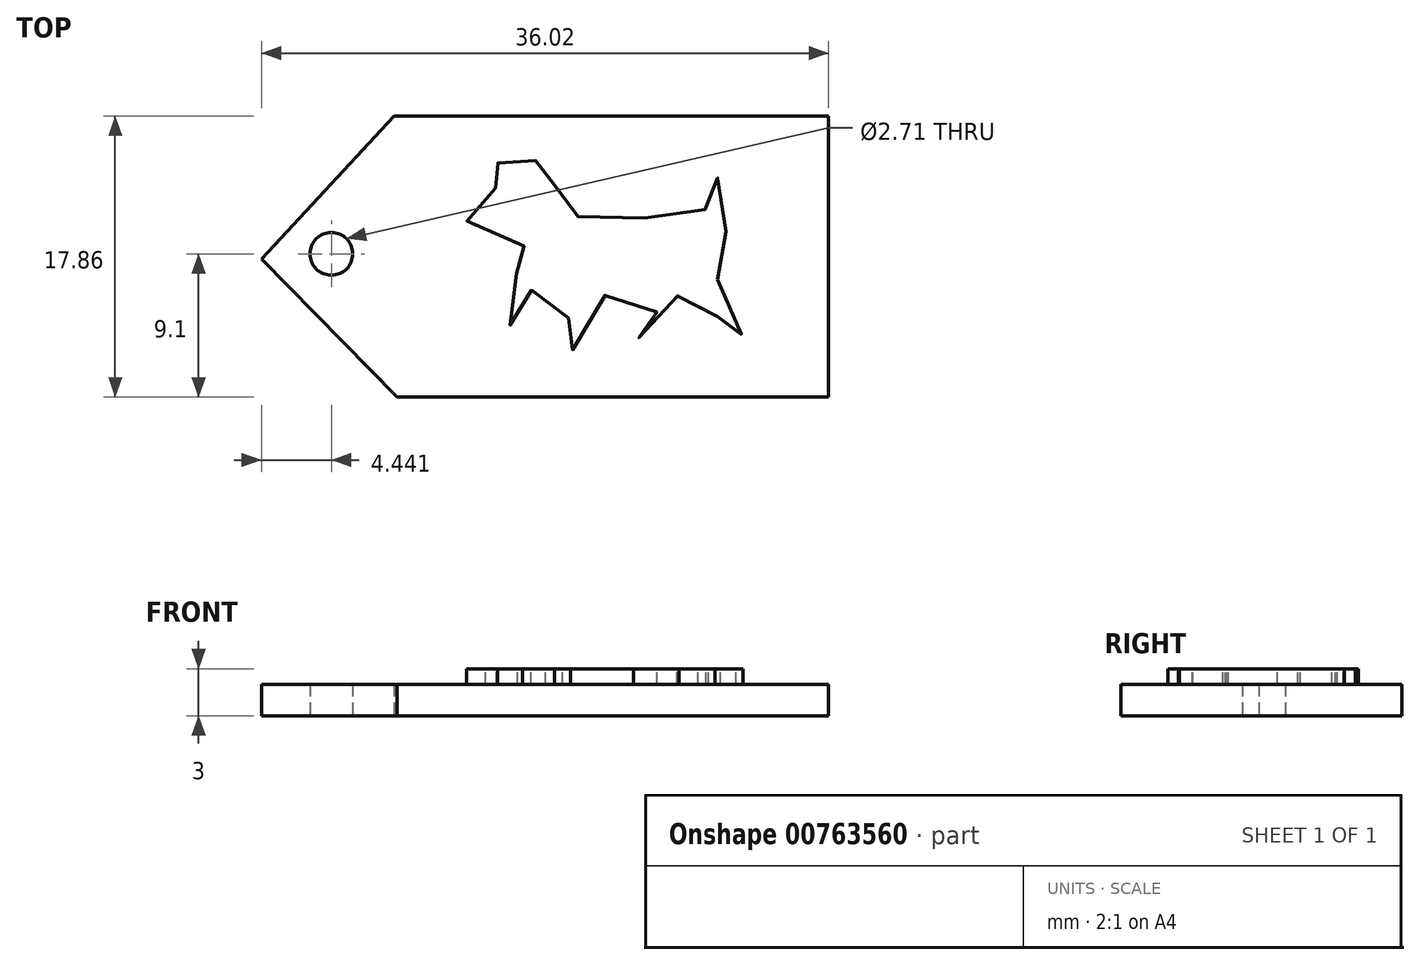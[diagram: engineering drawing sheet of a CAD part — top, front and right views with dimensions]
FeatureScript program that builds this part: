
annotation { "Feature Type Name" : "Feature", "Feature Type Description" : "" }
export const myFeature = defineFeature(function(context is Context, id is Id, definition is map)
    precondition{}
    {
        {
            var Q0;
            Q0=qCreatedBy(makeId("Top.planeOp"),FACE);
            var sketch = newSketch(context, id + "F0", { "sketchPlane" : qUnion([Q0])});
            skLineSegment(sketch, "E0", {"start": v(-27.58, 20.67) * mm, "end": v(0, 20.67) * mm});
            skLineSegment(sketch, "E1", {"start": v(0, 20.67) * mm, "end": v(0, 2.81) * mm});
            skLineSegment(sketch, "E2", {"start": v(0, 2.81) * mm, "end": v(-27.42, 2.81) * mm});
            skLineSegment(sketch, "E3", {"start": v(-27.42, 2.81) * mm, "end": v(-36.02, 11.58) * mm});
            skLineSegment(sketch, "E4", {"start": v(-36.02, 11.58) * mm, "end": v(-27.58, 20.67) * mm});
            skCircle(sketch, "E5", {"center": v(-31.58, 11.91) * mm, "radius": 1.36 * mm});
            skSolve(sketch);
        }
        {
            var Q0;
            Q0=makeQuery(id+"F0.imprint","IMPRINT",FACE,{"disambiguationData":[TD([[makeQuery(id+"F0.imprint","IMPRINT",EDGE,{"derivedFrom":sQuery(id+"F0.wireOp",EDGE,"E0")}),-1.0]])]});
            extrude(context, id + "F1", {"entities" : qUnion([Q0]), "depth" : 2 * mm, "offsetDistance" : 25 * mm});
        }
        {
            var Q0;
            Q0=qCreatedBy(makeId("Top.planeOp"),FACE);
            var sketch = newSketch(context, id + "F2", { "sketchPlane" : qUnion([Q0])});
            skFitSpline(sketch, "E6", {"points": [v(-17.4, 16.3) * mm, v(-16.98, 16.26) * mm, v(-16.95, 16.74) * mm, v(-17.56, 17.63) * mm, v(-18.61, 17.85) * mm, v(-19.34, 17.09) * mm, v(-19.76, 17) * mm, v(-20.33, 17.57) * mm, v(-20.94, 17.7) * mm, v(-21.58, 17.22) * mm, v(-21.74, 16.45) * mm, v(-21.39, 16.55) * mm, v(-21.13, 16.48) * mm, v(-21.16, 16.1) * mm, v(-21.32, 15.88) * mm, v(-21.67, 15.11) * mm, v(-22.66, 14.73) * mm, v(-23, 14.12) * mm, v(-21.86, 12.88) * mm, v(-19.95, 12.75) * mm, v(-19.38, 12.43) * mm, v(-19, 11.99) * mm, v(-18.93, 11.41) * mm, v(-18.9, 11.03) * mm, v(-19.22, 10.8) * mm, v(-19.95, 10.58) * mm, v(-20.68, 9.5) * mm, v(-20.97, 7.94) * mm, v(-20.05, 7.4) * mm, v(-19.44, 8) * mm, v(-19.76, 8.83) * mm, v(-19.38, 9.4) * mm, v(-18.55, 9.66) * mm, v(-17.65, 9.56) * mm, v(-16.44, 8.96) * mm, v(-16.57, 7.58) * mm, v(-16.7, 6.85) * mm, v(-17.37, 6.3) * mm, v(-17.27, 6.02) * mm, v(-15.9, 5.9) * mm, v(-15.2, 7.17) * mm, v(-14.46, 9.02) * mm, v(-14.11, 9.3) * mm, v(-13.16, 9.3) * mm, v(-11.91, 9.4) * mm, v(-10.9, 8.06) * mm, v(-11.37, 7.4) * mm, v(-11.98, 7.4) * mm, v(-12.3, 7.07) * mm, v(-12.36, 6.76) * mm, v(-10.77, 6.66) * mm, v(-9.55, 8.16) * mm, v(-9.55, 8.99) * mm, v(-9.59, 9.6) * mm, v(-8.79, 9.02) * mm, v(-7.54, 8.48) * mm, v(-6.97, 7.78) * mm, v(-6.87, 7.36) * mm, v(-7.2, 7.01) * mm, v(-6.84, 6.53) * mm, v(-5.5, 6.85) * mm, v(-5.98, 8.5) * mm, v(-6.27, 9.47) * mm, v(-7.03, 10.26) * mm, v(-7.7, 12.56) * mm, v(-7.74, 12.94) * mm, v(-6.84, 13.17) * mm, v(-6.01, 14) * mm, v(-5.92, 15.3) * mm, v(-6.5, 16.42) * mm, v(-8.25, 16.96) * mm, v(-7.86, 16.04) * mm, v(-7.64, 15.08) * mm, v(-8.12, 14.5) * mm, v(-9.27, 14.1) * mm, v(-10.54, 14.19) * mm, v(-12.49, 14.15) * mm, v(-13.83, 14.06) * mm, v(-15.49, 14.15) * mm, v(-16.63, 14.76) * mm, v(-17.88, 16.23) * mm, v(-17.94, 16.51) * mm, v(-17.4, 16.3) * mm]});
            skSolve(sketch);
        }
        {
            var Q0;
            Q0 = qSketchRegion(id + "F2", true);
            extrude(context, id + "F3", {"entities" : qUnion([Q0]), "operationType" : NewBodyOperationType.ADD, "depth" : 3 * mm, "offsetDistance" : 25 * mm});
        }
        {
            var Q0;
            Q0=qCreatedBy(makeId("Top.planeOp"),FACE);
            var sketch = newSketch(context, id + "F4", { "sketchPlane" : qUnion([Q0])});
            skCircle(sketch, "E7", {"center": v(-29, 12.03) * mm, "radius": 0.94 * mm});
            skSolve(sketch);
        }
        {
            var Q0;
            Q0 = qSketchRegion(id + "F4", true);
            extrude(context, id + "F5", {"entities" : qUnion([Q0]), "operationType" : NewBodyOperationType.REMOVE, "oppositeDirection" : true, "depth" : 2 * mm, "offsetDistance" : 25 * mm});
        }
    });
